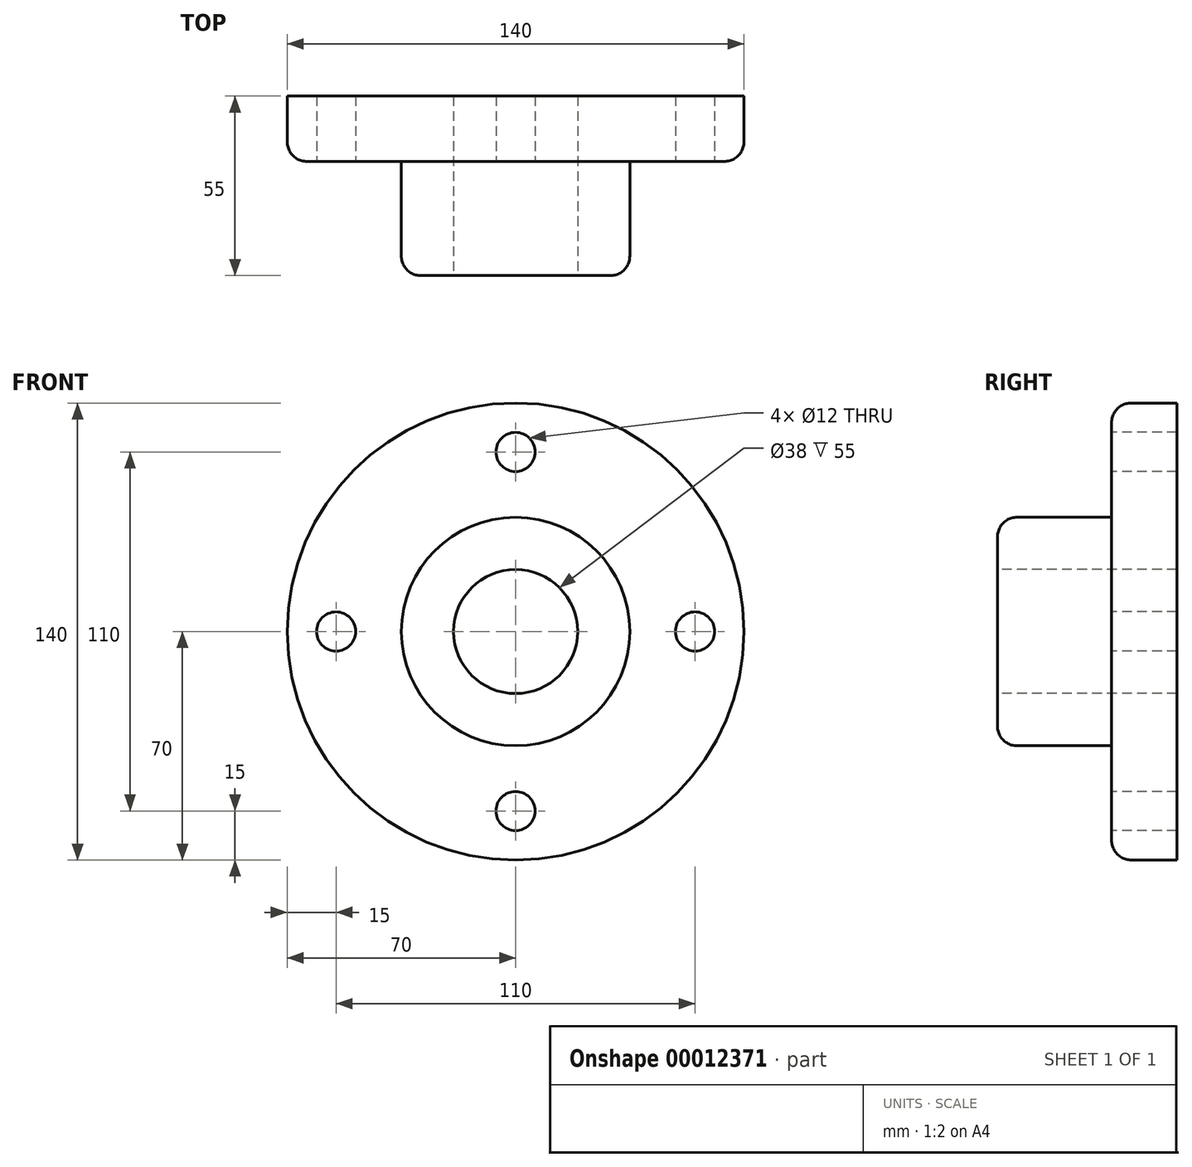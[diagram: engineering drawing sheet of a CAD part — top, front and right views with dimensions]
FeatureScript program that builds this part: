
annotation { "Feature Type Name" : "Feature", "Feature Type Description" : "" }
export const myFeature = defineFeature(function(context is Context, id is Id, definition is map)
    precondition{}
    {
        {
            var Q0;
            Q0=qCreatedBy(makeId("Front.planeOp"),FACE);
            var sketch = newSketch(context, id + "F0", { "sketchPlane" : qUnion([Q0])});
            skCircle(sketch, "E0", {"center": v(0, 0) * mm, "radius": 70 * mm});
            skSolve(sketch);
        }
        {
            var Q0;
            Q0=qCreatedBy(makeId("Top.planeOp"),FACE);
            var sketch = newSketch(context, id + "F1", { "sketchPlane" : qUnion([Q0])});
            skLineSegment(sketch, "E1", {"start": v(0, 27.47) * mm, "end": v(0, -42.47) * mm, "construction": true});
            skSolve(sketch);
        }
        {
            var Q0;
            Q0=qCreatedBy(makeId("Front.planeOp"),FACE);
            var sketch = newSketch(context, id + "F2", { "sketchPlane" : qUnion([Q0])});
            skCircle(sketch, "E2", {"center": v(0, 0) * mm, "radius": 35 * mm});
            skSolve(sketch);
        }
        {
            var Q0;
            Q0 = qSketchRegion(id + "F0", true);
            extrude(context, id + "F3", {"entities" : qUnion([Q0]), "oppositeDirection" : true, "depth" : 20 * mm});
        }
        {
            var Q0;
            Q0 = qSketchRegion(id + "F2", true);
            extrude(context, id + "F4", {"entities" : qUnion([Q0]), "operationType" : NewBodyOperationType.ADD, "depth" : 35 * mm});
        }
        {
            var Q0;
            Q0=makeQuery(id+"F4.opExtrude","CAP_FACE",FACE,{"disambiguationData":[OSD([sQuery(id+"F2.wireOp",EDGE,"E2")])],"isStart":false});
            var sketch = newSketch(context, id + "F5", { "sketchPlane" : qUnion([Q0])});
            skCircle(sketch, "E3", {"center": v(0, 0) * mm, "radius": 19 * mm});
            skSolve(sketch);
        }
        {
            var Q0;
            Q0 = qSketchRegion(id + "F5", true);
            extrude(context, id + "F6", {"entities" : qUnion([Q0]), "operationType" : NewBodyOperationType.REMOVE, "endBound" : BoundingType.THROUGH_ALL, "oppositeDirection" : true, "depth" : 25 * mm});
        }
        {
            var Q0;
            Q0=makeQuery(id+"F3.opExtrude","CAP_FACE",FACE,{"disambiguationData":[OSD([sQuery(id+"F0.wireOp",EDGE,"E0")])],"isStart":true});
            var sketch = newSketch(context, id + "F7", { "sketchPlane" : qUnion([Q0])});
            skCircle(sketch, "E4", {"center": v(0, 0) * mm, "radius": 55 * mm, "construction": true});
            skCircle(sketch, "E5", {"center": v(0, 55) * mm, "radius": 6 * mm});
            skSolve(sketch);
        }
        {
            var Q0;
            Q0 = qSketchRegion(id + "F7", true);
            extrude(context, id + "F8", {"entities" : qUnion([Q0]), "operationType" : NewBodyOperationType.REMOVE, "endBound" : BoundingType.THROUGH_ALL, "oppositeDirection" : true, "depth" : 25 * mm});
        }
        {
            var Q0;
            Q0=makeQuery(id+"F8.boolean.opBoolean","COPY",FACE,{"derivedFrom":makeQuery(id+"F8.opExtrude","SWEPT_FACE",FACE,{"disambiguationData":[OSD([sQuery(id+"F7.wireOp",EDGE,"E5")])]})});
            var Q1;
            Q1=sQuery(id+"F1.wireOp",EDGE,"E1");
            circularPattern(context, id + "F9", {"faces" : qUnion([Q0]), "axis" : qUnion([Q1]), "angle" : 360 * degree, "instanceCount" : 4, "equalSpace" : true, "patternType" : PatternType.FACE});
        }
        {
            var Q0;
            Q0=makeQuery(id+"F4.opExtrude","CAP_EDGE",EDGE,{"disambiguationData":[OSD([sQuery(id+"F2.wireOp",EDGE,"E2")])],"isStart":false});
            var Q1;
            Q1=makeQuery(id+"F4.opExtrude","CAP_EDGE",EDGE,{"disambiguationData":[OSD([sQuery(id+"F2.wireOp",EDGE,"E2")])],"isStart":true});
            var Q2;
            Q2=makeQuery(id+"F3.opExtrude","CAP_EDGE",EDGE,{"disambiguationData":[OSD([sQuery(id+"F0.wireOp",EDGE,"E0")])],"isStart":true});
            fillet(context, id + "F10", {"entities" : qUnion([Q0, Q1, Q2]), "radius" : 6 * mm, "tangentPropagation" : true, "allowEdgeOverflow" : false});
        }
    });
